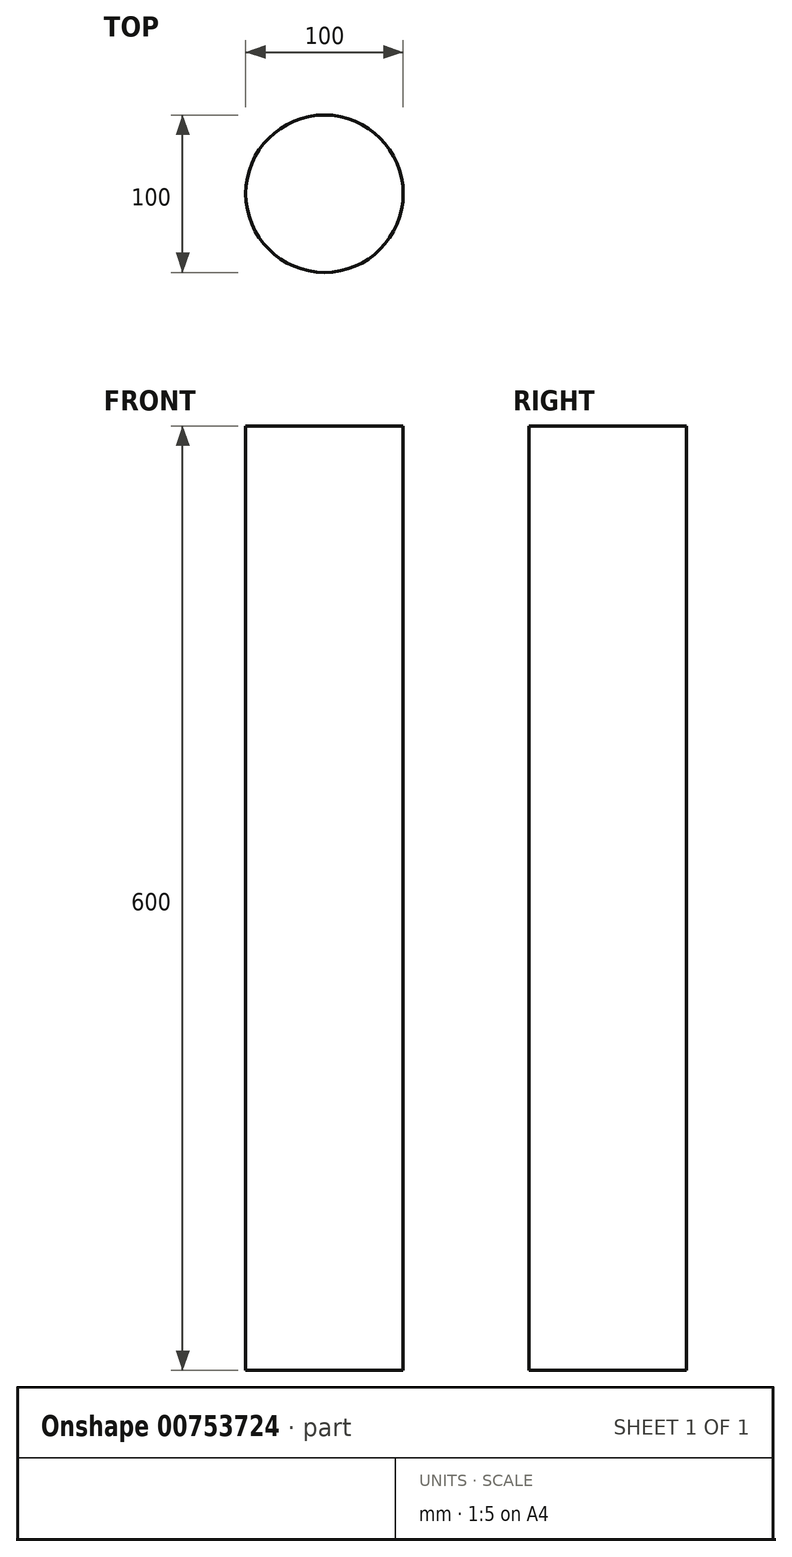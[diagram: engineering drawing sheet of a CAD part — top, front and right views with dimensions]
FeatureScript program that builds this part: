
annotation { "Feature Type Name" : "Feature", "Feature Type Description" : "" }
export const myFeature = defineFeature(function(context is Context, id is Id, definition is map)
    precondition{}
    {
        {
            var Q0;
            Q0=qCreatedBy(makeId("Top.planeOp"),FACE);
            var sketch = newSketch(context, id + "F0", { "sketchPlane" : qUnion([Q0])});
            skCircle(sketch, "E0", {"center": v(0, 0) * mm, "radius": 50 * mm});
            skSolve(sketch);
        }
        {
            var Q0;
            Q0=makeQuery(id+"F0.imprint","IMPRINT",FACE,{"disambiguationData":[TD([[makeQuery(id+"F0.imprint","IMPRINT",EDGE,{"derivedFrom":sQuery(id+"F0.wireOp",EDGE,"E0")}),1.0]])]});
            var Q1;
            Q1=sQuery(id+"F0.wireOp",EDGE,"E0");
            extrude(context, id + "F1", {"entities" : qUnion([Q0]), "bodyType" : ToolBodyType.SURFACE, "surfaceEntities" : qUnion([Q1]), "depth" : 600 * mm, "offsetDistance" : 25 * mm});
        }
    });
